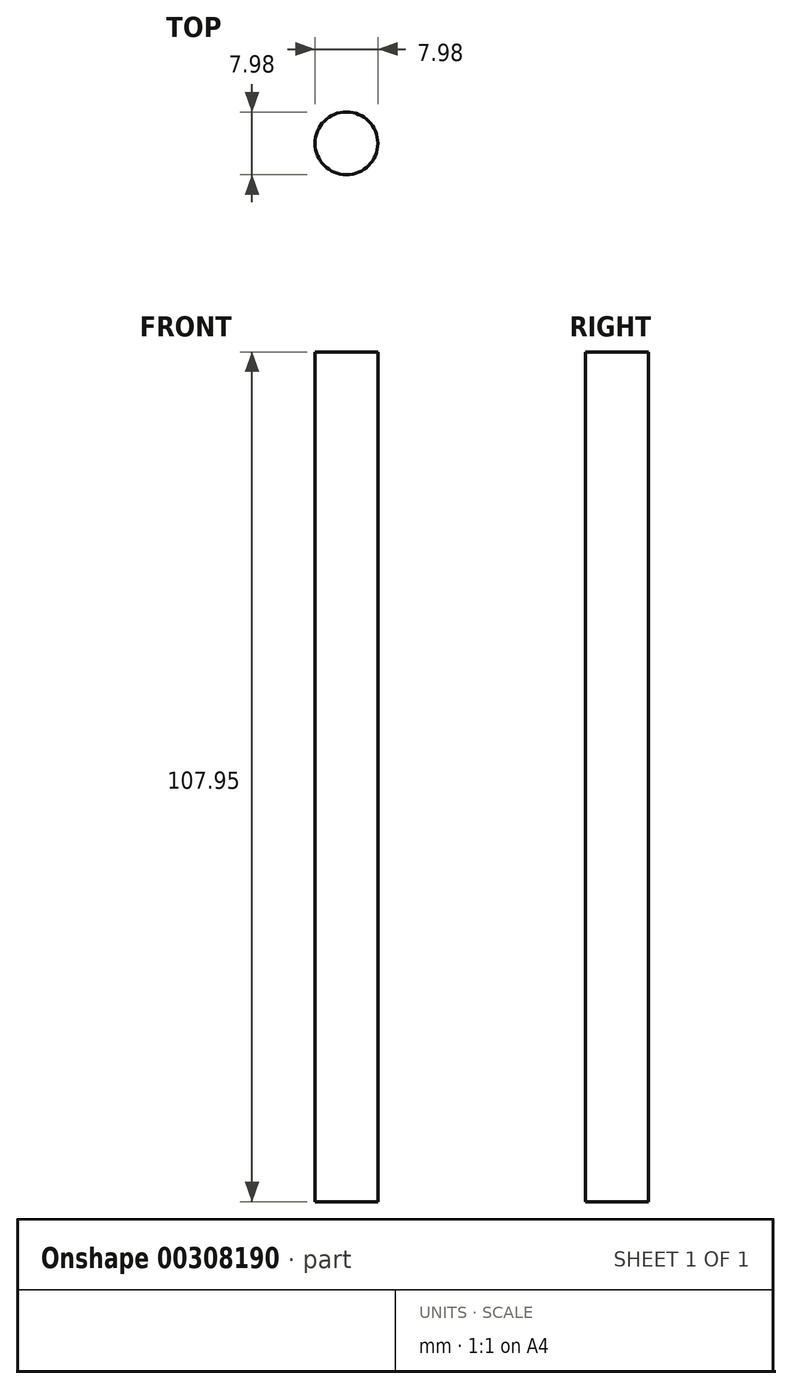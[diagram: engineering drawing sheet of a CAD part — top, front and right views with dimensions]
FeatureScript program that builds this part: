
annotation { "Feature Type Name" : "Feature", "Feature Type Description" : "" }
export const myFeature = defineFeature(function(context is Context, id is Id, definition is map)
    precondition{}
    {
        {
            var Q0;
            Q0=qCreatedBy(makeId("Top.planeOp"),FACE);
            var sketch = newSketch(context, id + "F0", { "sketchPlane" : qUnion([Q0])});
            skCircle(sketch, "E0", {"center": v(0, 0) * mm, "radius": 3.99 * mm});
            skSolve(sketch);
        }
        {
            var Q0;
            Q0 = qSketchRegion(id + "F0", true);
            extrude(context, id + "F1", {"entities" : qUnion([Q0]), "depth" : 107.95 * mm});
        }
    });
